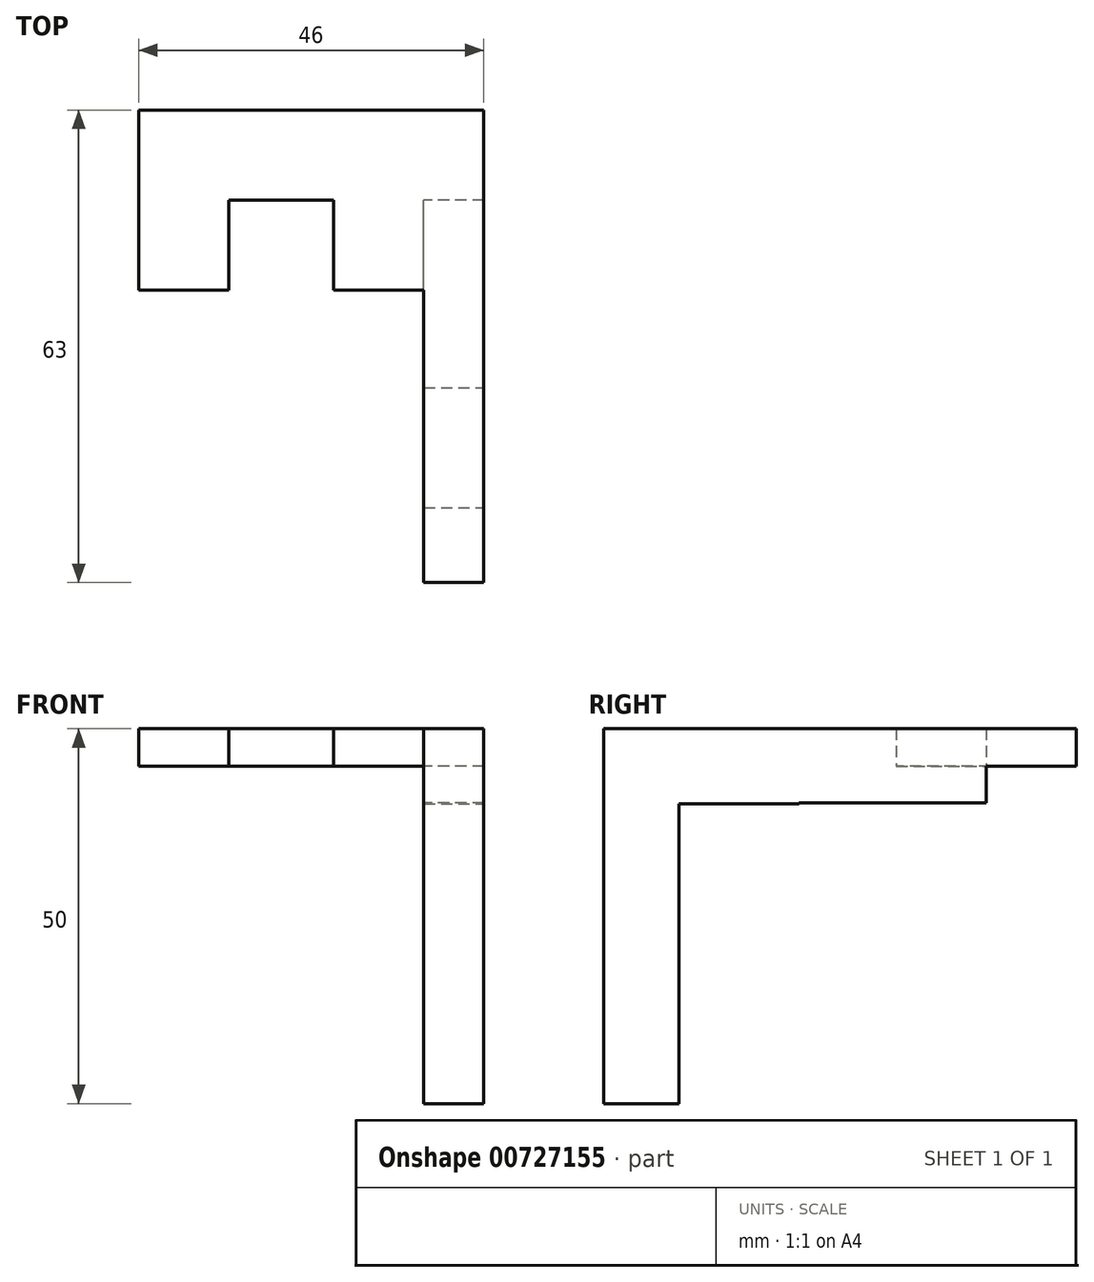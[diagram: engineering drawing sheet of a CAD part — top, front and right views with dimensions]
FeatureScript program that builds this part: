
annotation { "Feature Type Name" : "Feature", "Feature Type Description" : "" }
export const myFeature = defineFeature(function(context is Context, id is Id, definition is map)
    precondition{}
    {
        {
            var Q0;
            Q0=qCreatedBy(makeId("Top.planeOp"),FACE);
            var sketch = newSketch(context, id + "F0", { "sketchPlane" : qUnion([Q0])});
            skLineSegment(sketch, "E0.bottom", {"start": v(23, 6) * mm, "end": v(-23, 6) * mm});
            skLineSegment(sketch, "E0.top", {"start": v(23, -6) * mm, "end": v(-23, -6) * mm});
            skLineSegment(sketch, "E0.left", {"start": v(23, 6) * mm, "end": v(23, -6) * mm});
            skLineSegment(sketch, "E0.right", {"start": v(-23, 6) * mm, "end": v(-23, -6) * mm});
            skPoint(sketch, "E0.middle", {"position": v(0, 0) * mm});
            skSolve(sketch);
        }
        {
            var Q0;
            Q0=makeQuery(id+"F0.imprint","IMPRINT",FACE,{"disambiguationData":[TD([[makeQuery(id+"F0.imprint","IMPRINT",EDGE,{"derivedFrom":sQuery(id+"F0.wireOp",EDGE,"E0.bottom")}),1.0]])]});
            extrude(context, id + "F1", {"entities" : qUnion([Q0]), "depth" : 5 * mm, "offsetDistance" : 25 * mm});
        }
        {
            var Q0;
            Q0=makeQuery(id+"F1.opExtrude","SWEPT_FACE",FACE,{"disambiguationData":[OSD([sQuery(id+"F0.wireOp",EDGE,"E0.top")])]});
            var sketch = newSketch(context, id + "F2", { "sketchPlane" : qUnion([Q0])});
            skLineSegment(sketch, "E1.bottom", {"start": v(23, 5) * mm, "end": v(15, 5) * mm});
            skLineSegment(sketch, "E1.top", {"start": v(23, -45) * mm, "end": v(15, -45) * mm});
            skLineSegment(sketch, "E1.left", {"start": v(23, 5) * mm, "end": v(23, -45) * mm});
            skLineSegment(sketch, "E1.right", {"start": v(15, 5) * mm, "end": v(15, -45) * mm});
            skSolve(sketch);
        }
        {
            var Q0;
            Q0 = qSketchRegion(id + "F2", true);
            extrude(context, id + "F3", {"entities" : qUnion([Q0]), "operationType" : NewBodyOperationType.ADD, "depth" : 1 * mm, "offsetDistance" : 25 * mm});
        }
        {
            var Q0;
            Q0=makeQuery(id+"F3.opExtrude","CAP_FACE",FACE,{"disambiguationData":[OSD([sQuery(id+"F2.wireOp",EDGE,"E1.bottom"),sQuery(id+"F2.wireOp",EDGE,"E1.top"),sQuery(id+"F2.wireOp",EDGE,"E1.left"),sQuery(id+"F2.wireOp",EDGE,"E1.right")])],"isStart":false});
            extrude(context, id + "F4", {"entities" : qUnion([Q0]), "operationType" : NewBodyOperationType.ADD, "depth" : 50 * mm, "offsetDistance" : 25 * mm});
        }
        {
            var Q0;
            Q0=makeQuery(id+"F1.opExtrude","SWEPT_FACE",FACE,{"disambiguationData":[OSD([sQuery(id+"F0.wireOp",EDGE,"E0.top")])]});
            var sketch = newSketch(context, id + "F5", { "sketchPlane" : qUnion([Q0])});
            skLineSegment(sketch, "E2.bottom", {"start": v(-23, 5) * mm, "end": v(-11, 5) * mm});
            skLineSegment(sketch, "E2.top", {"start": v(-23, 0) * mm, "end": v(-11, 0) * mm});
            skLineSegment(sketch, "E2.left", {"start": v(-23, 5) * mm, "end": v(-23, 0) * mm});
            skLineSegment(sketch, "E2.right", {"start": v(-11, 5) * mm, "end": v(-11, 0) * mm});
            skSolve(sketch);
        }
        {
            var Q0;
            Q0=makeQuery(id+"F5.imprint","IMPRINT",FACE,{"disambiguationData":[TD([[makeQuery(id+"F5.imprint","IMPRINT",EDGE,{"derivedFrom":sQuery(id+"F5.wireOp",EDGE,"E2.bottom")}),1.0]])]});
            extrude(context, id + "F6", {"entities" : qUnion([Q0]), "operationType" : NewBodyOperationType.ADD, "depth" : 12 * mm, "offsetDistance" : 25 * mm});
        }
        {
            var Q0;
            Q0=makeQuery(id+"F1.opExtrude","SWEPT_FACE",FACE,{"disambiguationData":[OSD([sQuery(id+"F0.wireOp",EDGE,"E0.top")])]});
            var sketch = newSketch(context, id + "F7", { "sketchPlane" : qUnion([Q0])});
            skLineSegment(sketch, "E3.bottom", {"start": v(15, 5) * mm, "end": v(3, 5) * mm});
            skLineSegment(sketch, "E3.top", {"start": v(15, 0) * mm, "end": v(3, 0) * mm});
            skLineSegment(sketch, "E3.left", {"start": v(15, 5) * mm, "end": v(15, 0) * mm});
            skLineSegment(sketch, "E3.right", {"start": v(3, 5) * mm, "end": v(3, 0) * mm});
            skSolve(sketch);
        }
        {
            var Q0;
            Q0=makeQuery(id+"F7.imprint","IMPRINT",FACE,{"disambiguationData":[TD([[makeQuery(id+"F7.imprint","IMPRINT",EDGE,{"derivedFrom":sQuery(id+"F7.wireOp",EDGE,"E3.bottom")}),1.0]])]});
            extrude(context, id + "F8", {"entities" : qUnion([Q0]), "operationType" : NewBodyOperationType.ADD, "depth" : 12 * mm, "offsetDistance" : 25 * mm});
        }
        {
            var Q0;
            {var subQ0=sQuery(id+"F2.wireOp",EDGE,"E1.left");Q0=makeQuery(id+"F4.boolean.opBoolean","MERGE",FACE,{"derivedFrom":[makeQuery(id+"F3.boolean.opBoolean","MERGE",FACE,{"derivedFrom":[makeQuery(id+"F1.opExtrude","SWEPT_FACE",FACE,{"disambiguationData":[OSD([sQuery(id+"F0.wireOp",EDGE,"E0.left")])]}),makeQuery(id+"F3.opExtrude","SWEPT_FACE",FACE,{"disambiguationData":[OSD([subQ0])]})]}),makeQuery(id+"F4.opExtrude","SWEPT_FACE",FACE,{"disambiguationData":[OSD([subQ0])]})]});}
            var sketch = newSketch(context, id + "F9", { "sketchPlane" : qUnion([Q0])});
            skSolve(sketch);
        }
        {
            var Q0;
            {var subQ1=sQuery(id+"F0.wireOp",EDGE,"E0.left");Q0=makeQuery(id+"F9.imprint","IMPRINT",FACE,{"disambiguationData":[TD([[makeQuery(id+"F9.imprint","IMPRINT",EDGE,{"derivedFrom":makeQuery(id+"F1.opExtrude","CAP_EDGE",EDGE,{"disambiguationData":[OSD([subQ1])],"isStart":true})}),-1.0]])]});}
            var sketch = newSketch(context, id + "F10", { "sketchPlane" : qUnion([Q0])});
            skSolve(sketch);
        }
        {
            var Q0;
            {var subQ1=sQuery(id+"F0.wireOp",EDGE,"E0.left");Q0=makeQuery(id+"F9.imprint","IMPRINT",FACE,{"disambiguationData":[TD([[makeQuery(id+"F9.imprint","IMPRINT",EDGE,{"derivedFrom":makeQuery(id+"F1.opExtrude","CAP_EDGE",EDGE,{"disambiguationData":[OSD([subQ1])],"isStart":true})}),-1.0]])]});}
            var sketch = newSketch(context, id + "F11", { "sketchPlane" : qUnion([Q0])});
            skLineSegment(sketch, "E4", {"start": v(-47, -5) * mm, "end": v(-6.1, -5) * mm});
            skLineSegment(sketch, "E5", {"start": v(-6.1, -5) * mm, "end": v(-6.1, -45.03) * mm});
            skLineSegment(sketch, "E6", {"start": v(-6.1, -45.03) * mm, "end": v(-47, -45.03) * mm});
            skLineSegment(sketch, "E7", {"start": v(-47, -45.03) * mm, "end": v(-47, -5) * mm});
            skSolve(sketch);
        }
        {
            var Q0;
            Q0 = qSketchRegion(id + "F11", true);
            extrude(context, id + "F12", {"entities" : qUnion([Q0]), "operationType" : NewBodyOperationType.REMOVE, "endBound" : BoundingType.THROUGH_ALL, "oppositeDirection" : true, "depth" : 25 * mm, "offsetDistance" : 25 * mm});
        }
        {
            var Q0;
            Q0=makeQuery(id+"F3.opExtrude","CAP_FACE",FACE,{"disambiguationData":[OSD([sQuery(id+"F2.wireOp",EDGE,"E1.bottom"),sQuery(id+"F2.wireOp",EDGE,"E1.top"),sQuery(id+"F2.wireOp",EDGE,"E1.left"),sQuery(id+"F2.wireOp",EDGE,"E1.right")])],"isStart":true});
            var sketch = newSketch(context, id + "F13", { "sketchPlane" : qUnion([Q0])});
            skLineSegment(sketch, "E8", {"start": v(-23, -4.9) * mm, "end": v(-15, -4.9) * mm});
            skLineSegment(sketch, "E9", {"start": v(-15, -4.9) * mm, "end": v(-15, -45) * mm});
            skLineSegment(sketch, "E10", {"start": v(-15, -45) * mm, "end": v(-23, -45) * mm});
            skLineSegment(sketch, "E11", {"start": v(-23, -45) * mm, "end": v(-23, -4.9) * mm});
            skSolve(sketch);
        }
        {
            var Q0;
            Q0=makeQuery(id+"F13.imprint","IMPRINT",FACE,{"disambiguationData":[TD([[makeQuery(id+"F13.imprint","IMPRINT",EDGE,{"derivedFrom":sQuery(id+"F13.wireOp",EDGE,"E8")}),-1.0]])]});
            extrude(context, id + "F14", {"entities" : qUnion([Q0]), "operationType" : NewBodyOperationType.REMOVE, "oppositeDirection" : true, "depth" : 25 * mm, "offsetDistance" : 25 * mm});
        }
    });
